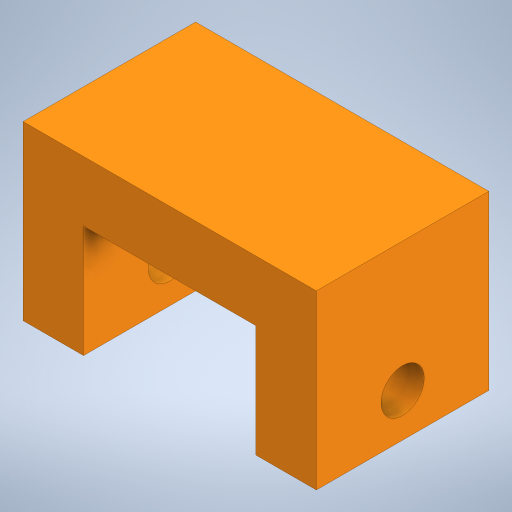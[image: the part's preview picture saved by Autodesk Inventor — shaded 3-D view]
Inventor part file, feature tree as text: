
AUTODESK INVENTOR PART (.ipt)
format: ipt  version: 2023 (Build 270158000, 158)  size: 194,560 bytes
history: native  units: mm
features: extrude x2, sketch x2
ambient origin geometry x8: Origin, YZ Plane, XZ Plane, XY Plane, X Axis, Y Axis, Z Axis, Center Point
bodies: Solid1 (feature_tree)
feature tree (4):
  extrude  "Extrusion1"  Depth=7.0mm
  extrude  "Extrusion2"  Depth=7.0mm
  sketch  "Sketch1"  dims[d0=34.0mm d1=7.0mm]
  sketch  "Sketch2"  dims[d2=7.0mm d3=7.0mm d4=13.0mm d5=20.0mm d6=0.0mm d7=5.0mm d8=10.0mm d9=5.0mm d10=60.0mm d11=10.0mm d12=0.0mm d13=0.0mm]
